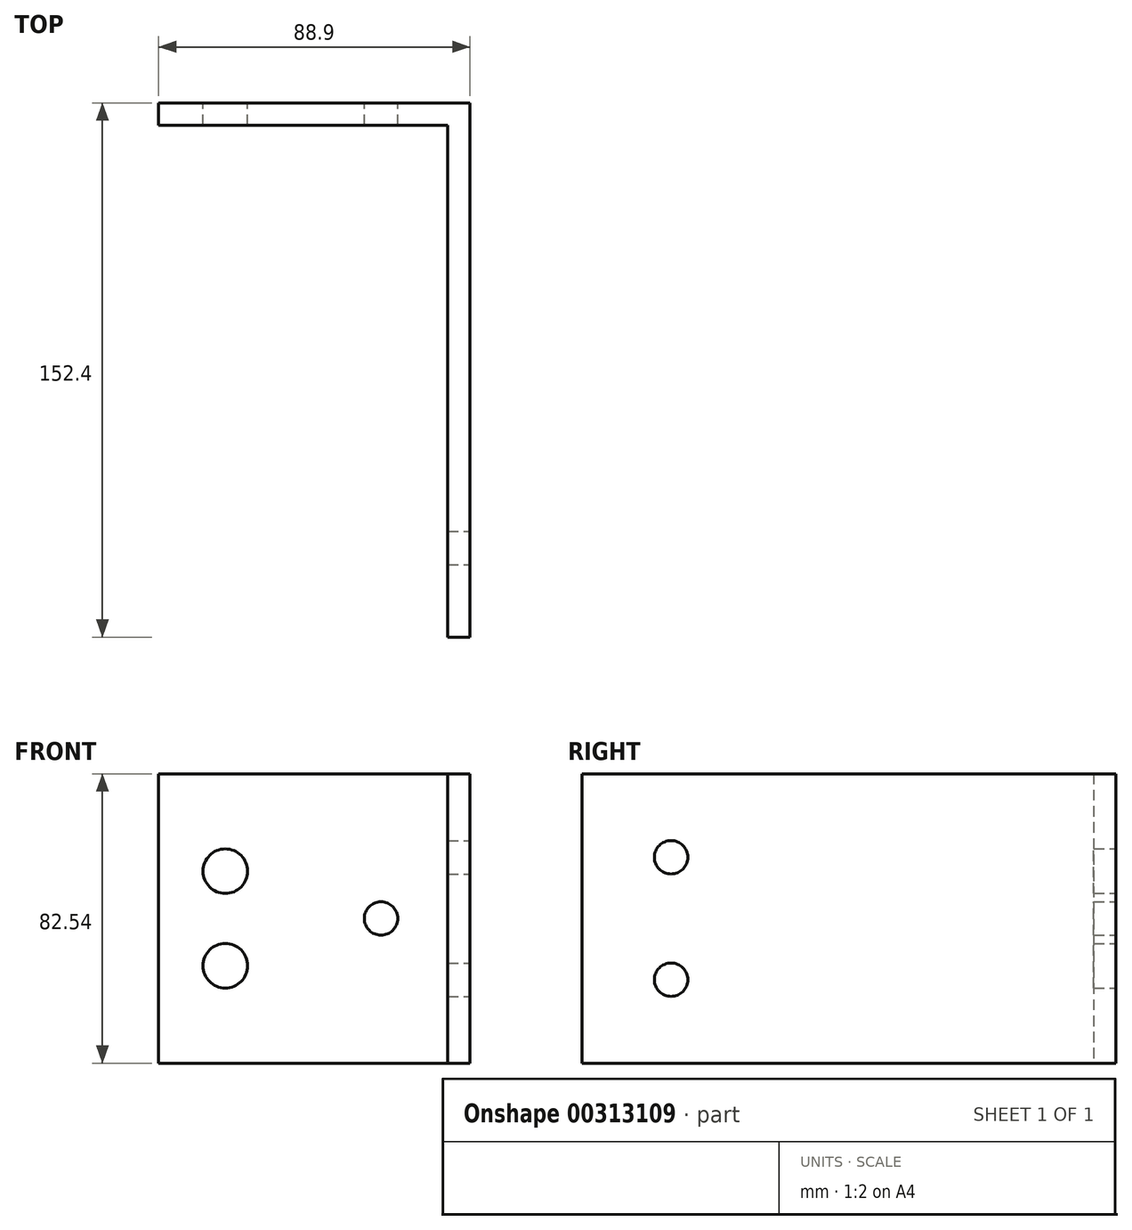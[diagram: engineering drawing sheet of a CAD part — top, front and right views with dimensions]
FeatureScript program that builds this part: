
annotation { "Feature Type Name" : "Feature", "Feature Type Description" : "" }
export const myFeature = defineFeature(function(context is Context, id is Id, definition is map)
    precondition{}
    {
        {
            var Q0;
            Q0=qCreatedBy(makeId("Top.planeOp"),FACE);
            var sketch = newSketch(context, id + "F0", { "sketchPlane" : qUnion([Q0])});
            skLineSegment(sketch, "E0", {"start": v(0, 0) * mm, "end": v(-82.55, 0) * mm});
            skLineSegment(sketch, "E1", {"start": v(-82.55, 0) * mm, "end": v(-82.55, 6.35) * mm});
            skLineSegment(sketch, "E2", {"start": v(-82.55, 6.35) * mm, "end": v(6.35, 6.35) * mm});
            skLineSegment(sketch, "E3", {"start": v(6.35, 6.35) * mm, "end": v(6.35, -146.05) * mm});
            skLineSegment(sketch, "E4", {"start": v(6.35, -146.05) * mm, "end": v(0, -146.05) * mm});
            skLineSegment(sketch, "E5", {"start": v(0, -146.05) * mm, "end": v(0, 0) * mm});
            skSolve(sketch);
        }
        {
            var Q0;
            Q0=qSketchRegion(id+"F0",true);
            extrude(context, id + "F1", {"entities" : qUnion([Q0]), "endBound" : BoundingType.SYMMETRIC, "depth" : 82.55 * mm});
        }
        {
            var Q0;
            Q0=makeQuery(id+"F1.opExtrude","SWEPT_FACE",FACE,{"disambiguationData":[OSD([sQuery(id+"F0.wireOp",EDGE,"E3")])]});
            var sketch = newSketch(context, id + "F2", { "sketchPlane" : qUnion([Q0])});
            skCircle(sketch, "E6", {"center": v(-120.65, 17.46) * mm, "radius": 4.76 * mm});
            skCircle(sketch, "E7", {"center": v(-120.65, -17.46) * mm, "radius": 4.76 * mm});
            skLineSegment(sketch, "E8", {"start": v(-120.65, 17.46) * mm, "end": v(-120.65, -17.46) * mm, "construction": true});
            skPoint(sketch, "E9", {"position": v(-120.65, 0) * mm});
            skSolve(sketch);
        }
        {
            var Q0;
            Q0=qSketchRegion(id+"F2",true);
            extrude(context, id + "F3", {"entities" : qUnion([Q0]), "operationType" : NewBodyOperationType.REMOVE, "endBound" : BoundingType.THROUGH_ALL, "oppositeDirection" : true, "depth" : 25.4 * mm});
        }
        {
            var Q0;
            Q0=makeQuery(id+"F1.opExtrude","SWEPT_FACE",FACE,{"disambiguationData":[OSD([sQuery(id+"F0.wireOp",EDGE,"E2")])]});
            var sketch = newSketch(context, id + "F4", { "sketchPlane" : qUnion([Q0])});
            skCircle(sketch, "E10", {"center": v(63.5, 13.49) * mm, "radius": 6.35 * mm});
            skCircle(sketch, "E11", {"center": v(63.5, -13.49) * mm, "radius": 6.35 * mm});
            skLineSegment(sketch, "E12", {"start": v(63.5, 13.49) * mm, "end": v(63.5, -13.49) * mm, "construction": true});
            skPoint(sketch, "E13", {"position": v(63.5, 0) * mm});
            skCircle(sketch, "E14", {"center": v(19.05, 0) * mm, "radius": 4.76 * mm});
            skSolve(sketch);
        }
        {
            var Q0;
            Q0=qSketchRegion(id+"F4",true);
            extrude(context, id + "F5", {"entities" : qUnion([Q0]), "operationType" : NewBodyOperationType.REMOVE, "endBound" : BoundingType.THROUGH_ALL, "oppositeDirection" : true, "depth" : 25.4 * mm});
        }
    });
